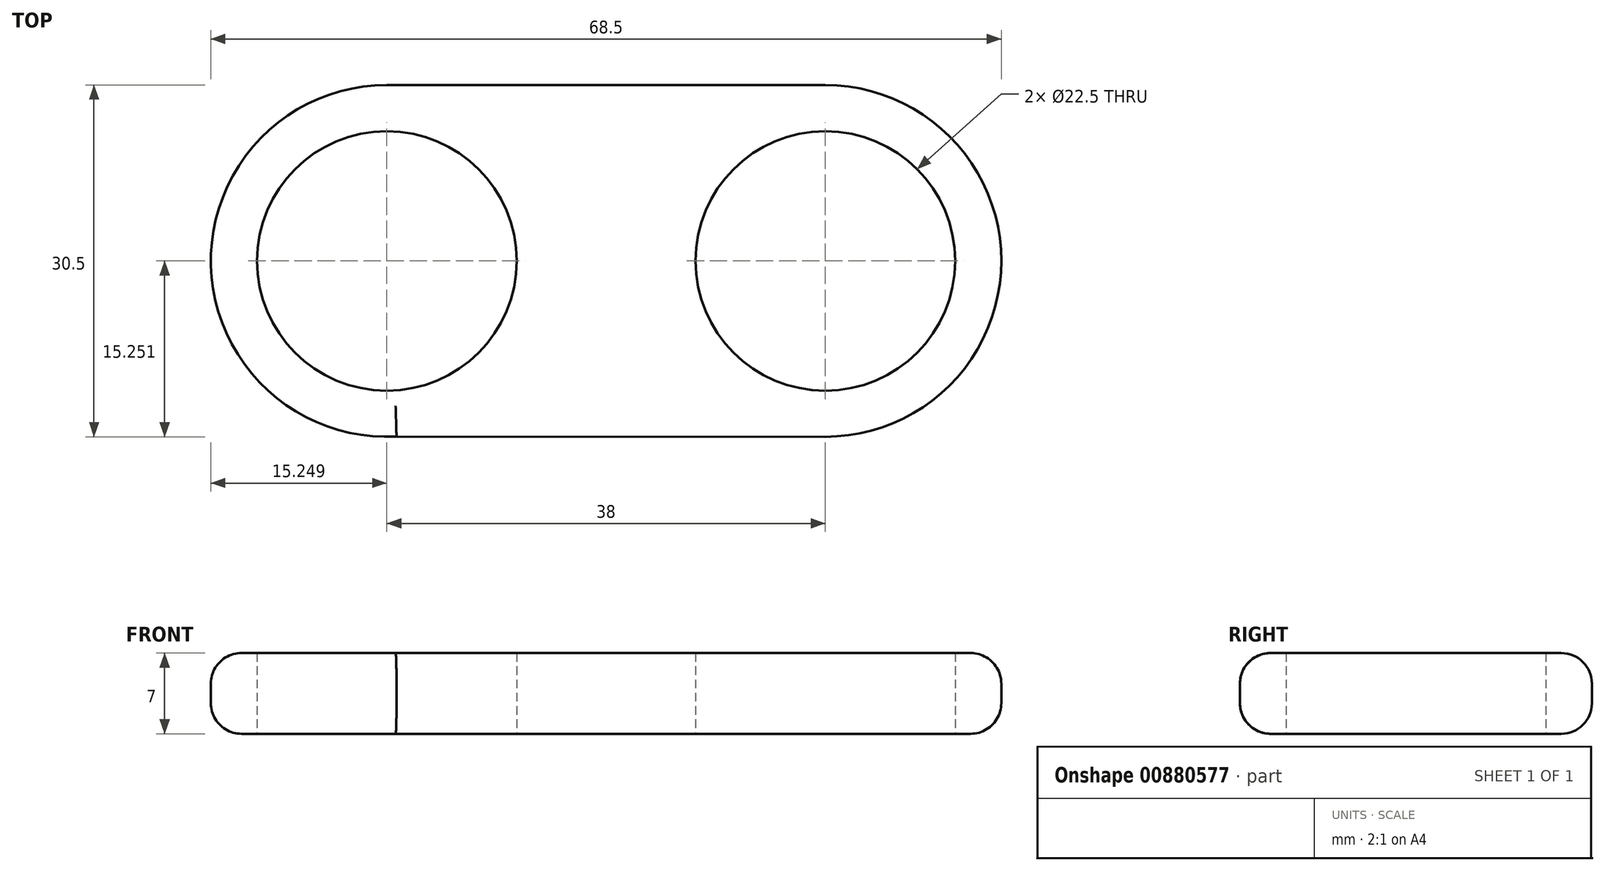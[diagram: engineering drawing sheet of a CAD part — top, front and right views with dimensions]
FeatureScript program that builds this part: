
annotation { "Feature Type Name" : "Feature", "Feature Type Description" : "" }
export const myFeature = defineFeature(function(context is Context, id is Id, definition is map)
    precondition{}
    {
        {
            var Q0;
            Q0=qCreatedBy(makeId("Top.planeOp"),FACE);
            var sketch = newSketch(context, id + "F0", { "sketchPlane" : qUnion([Q0])});
            skCircle(sketch, "E0", {"center": v(-44.16, 12.18) * mm, "radius": 11.25 * mm});
            skCircle(sketch, "E1", {"center": v(-6.16, 12.18) * mm, "radius": 11.25 * mm});
            skCircle(sketch, "E2.0", {"center": v(-44.16, 12.18) * mm, "radius": 15.25 * mm});
            skCircle(sketch, "E3.0", {"center": v(-6.16, 12.18) * mm, "radius": 15.25 * mm});
            skLineSegment(sketch, "E4", {"start": v(-43.32, -3.05) * mm, "end": v(-6.17, -3.07) * mm});
            skLineSegment(sketch, "E5", {"start": v(-44.16, 12.18) * mm, "end": v(-44.16, 30.42) * mm, "construction": true});
            skLineSegment(sketch, "E6", {"start": v(-44.16, 27.43) * mm, "end": v(0.63, 27.43) * mm});
            skLineSegment(sketch, "E7", {"start": v(-44.16, 12.18) * mm, "end": v(-6.16, 12.18) * mm});
            skSolve(sketch);
        }
        {
            var Q0;
            Q0=makeQuery(id+"F0.imprint","IMPRINT",FACE,{"disambiguationData":[TD([[makeQuery(id+"F0.imprint","IMPRINT",EDGE,{"derivedFrom":sQuery(id+"F0.wireOp",EDGE,"E0")}),-1.0]])]});
            var Q1;
            Q1=makeQuery(id+"F0.imprint","IMPRINT",FACE,{"disambiguationData":[TD([[makeQuery(id+"F0.imprint","IMPRINT",EDGE,{"derivedFrom":sQuery(id+"F0.wireOp",EDGE,"E1")}),-1.0]])]});
            var Q2;
            {var subQ3=sQuery(id+"F0.wireOp",EDGE,"E4");Q2=makeQuery(id+"F0.imprint","IMPRINT",FACE,{"disambiguationData":[TD([[makeQuery(id+"F0.imprint","IMPRINT",EDGE,{"derivedFrom":subQ3}),1.0]])]});}
            extrude(context, id + "F1", {"entities" : qUnion([Q0, Q1, Q2]), "depth" : 7 * mm, "offsetDistance" : 25 * mm});
        }
        {
            var Q0;
            Q0 = qSketchRegion(id + "F0", true);
            extrude(context, id + "F2", {"entities" : qUnion([Q0]), "operationType" : NewBodyOperationType.ADD, "depth" : 7 * mm, "offsetDistance" : 25 * mm});
        }
        {
            var Q0;
            Q0=makeQuery(id+"F1.opExtrude","CAP_EDGE",EDGE,{"disambiguationData":[OSD([sQuery(id+"F0.wireOp",EDGE,"E4")])],"isStart":false});
            var Q1;
            Q1=makeQuery(id+"F1.opExtrude","CAP_EDGE",EDGE,{"disambiguationData":[OSD([sQuery(id+"F0.wireOp",EDGE,"E3.0")])],"isStart":false});
            var Q2;
            Q2=makeQuery(id+"F2.boolean.opBoolean","SPLIT",EDGE,{"derivedFrom":makeQuery(id+"F1.opExtrude","CAP_EDGE",EDGE,{"disambiguationData":[OSD([sQuery(id+"F0.wireOp",EDGE,"OZNTtckA-S4kU-fLOx-9SOZ-5cdnNS4EbmOT")])],"isStart":false})});
            var Q3;
            Q3=makeQuery(id+"F1.opExtrude","CAP_EDGE",EDGE,{"disambiguationData":[OSD([sQuery(id+"F0.wireOp",EDGE,"E2.0")])],"isStart":false});
            var Q4;
            Q4=makeQuery(id+"F1.opExtrude","CAP_EDGE",EDGE,{"disambiguationData":[OSD([sQuery(id+"F0.wireOp",EDGE,"E2.0")])],"isStart":true});
            var Q5;
            Q5=makeQuery(id+"F1.opExtrude","CAP_EDGE",EDGE,{"disambiguationData":[OSD([sQuery(id+"F0.wireOp",EDGE,"E4")])],"isStart":true});
            var Q6;
            Q6=makeQuery(id+"F2.boolean.opBoolean","SPLIT",EDGE,{"derivedFrom":makeQuery(id+"F1.opExtrude","CAP_EDGE",EDGE,{"disambiguationData":[OSD([sQuery(id+"F0.wireOp",EDGE,"OZNTtckA-S4kU-fLOx-9SOZ-5cdnNS4EbmOT")])],"isStart":true})});
            var Q7;
            Q7=makeQuery(id+"F1.opExtrude","CAP_EDGE",EDGE,{"disambiguationData":[OSD([sQuery(id+"F0.wireOp",EDGE,"E3.0")])],"isStart":true});
            fillet(context, id + "F3", {"entities" : qUnion([Q0, Q1, Q2, Q3, Q4, Q5, Q6, Q7]), "radius" : 2.66 * mm, "tangentPropagation" : true, "allowEdgeOverflow" : false});
        }
    });
